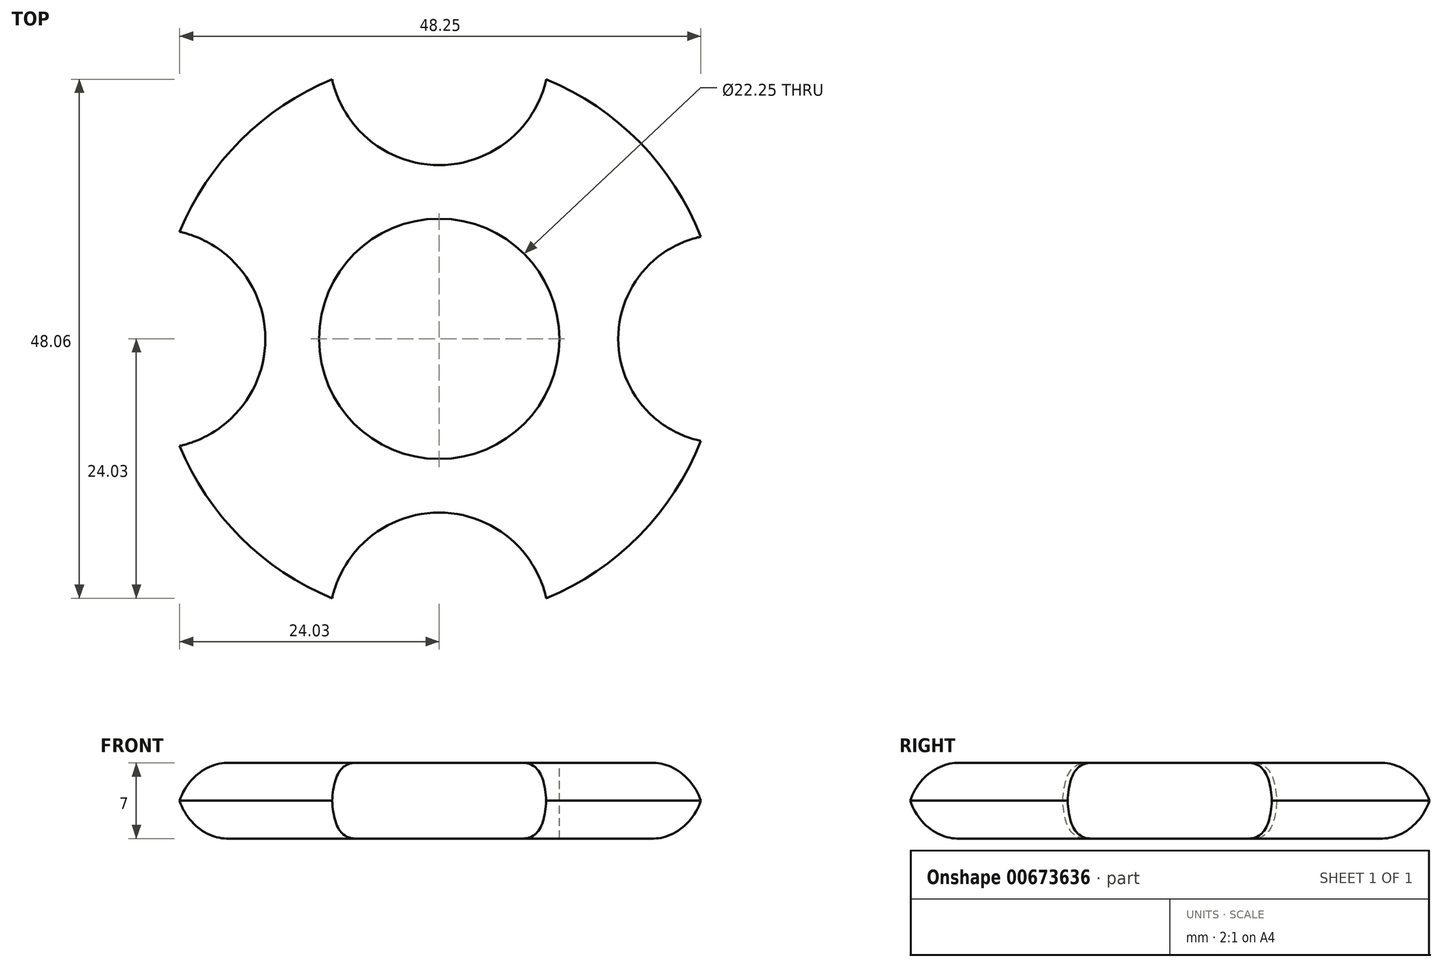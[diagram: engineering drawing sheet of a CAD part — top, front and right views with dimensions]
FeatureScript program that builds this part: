
annotation { "Feature Type Name" : "Feature", "Feature Type Description" : "" }
export const myFeature = defineFeature(function(context is Context, id is Id, definition is map)
    precondition{}
    {
        {
            var Q0;
            Q0=qCreatedBy(makeId("Top.planeOp"),FACE);
            var sketch = newSketch(context, id + "F0", { "sketchPlane" : qUnion([Q0])});
            skCircle(sketch, "E0", {"center": v(0, 0) * mm, "radius": 26.25 * mm});
            skSolve(sketch);
        }
        {
            var Q0;
            Q0 = qSketchRegion(id + "F0", true);
            extrude(context, id + "F1", {"entities" : qUnion([Q0]), "depth" : 7 * mm, "offsetDistance" : 25.4 * mm});
        }
        {
            var Q0;
            Q0=makeQuery(id+"F1.opExtrude","CAP_FACE",FACE,{"disambiguationData":[OSD([sQuery(id+"F0.wireOp",EDGE,"E0")])],"isStart":false});
            var sketch = newSketch(context, id + "F2", { "sketchPlane" : qUnion([Q0])});
            skCircle(sketch, "E1", {"center": v(0, 0) * mm, "radius": 11.13 * mm});
            skSolve(sketch);
        }
        {
            var Q0;
            Q0 = qSketchRegion(id + "F2", true);
            extrude(context, id + "F3", {"entities" : qUnion([Q0]), "operationType" : NewBodyOperationType.REMOVE, "oppositeDirection" : true, "depth" : 25.4 * mm, "offsetDistance" : 25.4 * mm});
        }
        {
            var Q0;
            Q0=makeQuery(id+"F1.opExtrude","CAP_FACE",FACE,{"disambiguationData":[OSD([sQuery(id+"F0.wireOp",EDGE,"E0")])],"isStart":false});
            var sketch = newSketch(context, id + "F4", { "sketchPlane" : qUnion([Q0])});
            skCircle(sketch, "E2", {"center": v(0, -26.25) * mm, "radius": 10.16 * mm});
            skCircle(sketch, "E3", {"center": v(-26.25, 0) * mm, "radius": 10.16 * mm});
            skCircle(sketch, "E4", {"center": v(0, 26.25) * mm, "radius": 10.16 * mm});
            skCircle(sketch, "E5", {"center": v(26.25, 0) * mm, "radius": 9.67 * mm});
            skSolve(sketch);
        }
        {
            var Q0;
            Q0 = qSketchRegion(id + "F4", true);
            extrude(context, id + "F5", {"entities" : qUnion([Q0]), "operationType" : NewBodyOperationType.REMOVE, "oppositeDirection" : true, "depth" : 25.4 * mm, "offsetDistance" : 25.4 * mm});
        }
        {
            var Q0;
            {var subQ0=sQuery(id+"F0.wireOp",EDGE,"E0");Q0=makeQuery(id+"F5.boolean.opBoolean","SPLIT",EDGE,{"disambiguationData":[TD([makeQuery(id+"F1.opExtrude","SWEPT_FACE",FACE,{"disambiguationData":[OSD([subQ0])]}),makeQuery(id+"F1.opExtrude","CAP_FACE",FACE,{"disambiguationData":[OSD([subQ0])],"isStart":true}),makeQuery(id+"F5.opExtrude","SWEPT_FACE",FACE,{"disambiguationData":[OSD([sQuery(id+"F4.wireOp",EDGE,"E2")])]}),makeQuery(id+"F5.opExtrude","SWEPT_FACE",FACE,{"disambiguationData":[OSD([sQuery(id+"F4.wireOp",EDGE,"E5")])]})])],"derivedFrom":makeQuery(id+"F1.opExtrude","CAP_EDGE",EDGE,{"disambiguationData":[OSD([subQ0])],"isStart":true})});}
            var Q1;
            {var subQ0=sQuery(id+"F0.wireOp",EDGE,"E0");Q1=makeQuery(id+"F5.boolean.opBoolean","SPLIT",EDGE,{"disambiguationData":[TD([makeQuery(id+"F1.opExtrude","SWEPT_FACE",FACE,{"disambiguationData":[OSD([subQ0])]}),makeQuery(id+"F1.opExtrude","CAP_FACE",FACE,{"disambiguationData":[OSD([subQ0])],"isStart":true}),makeQuery(id+"F5.opExtrude","SWEPT_FACE",FACE,{"disambiguationData":[OSD([sQuery(id+"F4.wireOp",EDGE,"E2")])]}),makeQuery(id+"F5.opExtrude","SWEPT_FACE",FACE,{"disambiguationData":[OSD([sQuery(id+"F4.wireOp",EDGE,"E3")])]})])],"derivedFrom":makeQuery(id+"F1.opExtrude","CAP_EDGE",EDGE,{"disambiguationData":[OSD([subQ0])],"isStart":true})});}
            var Q2;
            {var subQ0=sQuery(id+"F0.wireOp",EDGE,"E0");Q2=makeQuery(id+"F5.boolean.opBoolean","SPLIT",EDGE,{"disambiguationData":[TD([makeQuery(id+"F1.opExtrude","SWEPT_FACE",FACE,{"disambiguationData":[OSD([subQ0])]}),makeQuery(id+"F1.opExtrude","CAP_FACE",FACE,{"disambiguationData":[OSD([subQ0])],"isStart":true}),makeQuery(id+"F5.opExtrude","SWEPT_FACE",FACE,{"disambiguationData":[OSD([sQuery(id+"F4.wireOp",EDGE,"E3")])]}),makeQuery(id+"F5.opExtrude","SWEPT_FACE",FACE,{"disambiguationData":[OSD([sQuery(id+"F4.wireOp",EDGE,"E4")])]})])],"derivedFrom":makeQuery(id+"F1.opExtrude","CAP_EDGE",EDGE,{"disambiguationData":[OSD([subQ0])],"isStart":true})});}
            var Q3;
            {var subQ0=sQuery(id+"F0.wireOp",EDGE,"E0");Q3=makeQuery(id+"F5.boolean.opBoolean","SPLIT",EDGE,{"disambiguationData":[TD([makeQuery(id+"F1.opExtrude","SWEPT_FACE",FACE,{"disambiguationData":[OSD([subQ0])]}),makeQuery(id+"F1.opExtrude","CAP_FACE",FACE,{"disambiguationData":[OSD([subQ0])],"isStart":false}),makeQuery(id+"F5.opExtrude","SWEPT_FACE",FACE,{"disambiguationData":[OSD([sQuery(id+"F4.wireOp",EDGE,"E3")])]}),makeQuery(id+"F5.opExtrude","SWEPT_FACE",FACE,{"disambiguationData":[OSD([sQuery(id+"F4.wireOp",EDGE,"E4")])]})])],"derivedFrom":makeQuery(id+"F1.opExtrude","CAP_EDGE",EDGE,{"disambiguationData":[OSD([subQ0])],"isStart":false})});}
            var Q4;
            {var subQ0=sQuery(id+"F0.wireOp",EDGE,"E0");Q4=makeQuery(id+"F5.boolean.opBoolean","SPLIT",EDGE,{"disambiguationData":[TD([makeQuery(id+"F1.opExtrude","SWEPT_FACE",FACE,{"disambiguationData":[OSD([subQ0])]}),makeQuery(id+"F1.opExtrude","CAP_FACE",FACE,{"disambiguationData":[OSD([subQ0])],"isStart":false}),makeQuery(id+"F5.opExtrude","SWEPT_FACE",FACE,{"disambiguationData":[OSD([sQuery(id+"F4.wireOp",EDGE,"E2")])]}),makeQuery(id+"F5.opExtrude","SWEPT_FACE",FACE,{"disambiguationData":[OSD([sQuery(id+"F4.wireOp",EDGE,"E3")])]})])],"derivedFrom":makeQuery(id+"F1.opExtrude","CAP_EDGE",EDGE,{"disambiguationData":[OSD([subQ0])],"isStart":false})});}
            var Q5;
            {var subQ0=sQuery(id+"F0.wireOp",EDGE,"E0");Q5=makeQuery(id+"F5.boolean.opBoolean","SPLIT",EDGE,{"disambiguationData":[TD([makeQuery(id+"F1.opExtrude","SWEPT_FACE",FACE,{"disambiguationData":[OSD([subQ0])]}),makeQuery(id+"F1.opExtrude","CAP_FACE",FACE,{"disambiguationData":[OSD([subQ0])],"isStart":false}),makeQuery(id+"F5.opExtrude","SWEPT_FACE",FACE,{"disambiguationData":[OSD([sQuery(id+"F4.wireOp",EDGE,"E2")])]}),makeQuery(id+"F5.opExtrude","SWEPT_FACE",FACE,{"disambiguationData":[OSD([sQuery(id+"F4.wireOp",EDGE,"E5")])]})])],"derivedFrom":makeQuery(id+"F1.opExtrude","CAP_EDGE",EDGE,{"disambiguationData":[OSD([subQ0])],"isStart":false})});}
            var Q6;
            {var subQ0=sQuery(id+"F0.wireOp",EDGE,"E0");Q6=makeQuery(id+"F5.boolean.opBoolean","SPLIT",EDGE,{"disambiguationData":[TD([makeQuery(id+"F1.opExtrude","SWEPT_FACE",FACE,{"disambiguationData":[OSD([subQ0])]}),makeQuery(id+"F1.opExtrude","CAP_FACE",FACE,{"disambiguationData":[OSD([subQ0])],"isStart":false}),makeQuery(id+"F5.opExtrude","SWEPT_FACE",FACE,{"disambiguationData":[OSD([sQuery(id+"F4.wireOp",EDGE,"E4")])]}),makeQuery(id+"F5.opExtrude","SWEPT_FACE",FACE,{"disambiguationData":[OSD([sQuery(id+"F4.wireOp",EDGE,"E5")])]})])],"derivedFrom":makeQuery(id+"F1.opExtrude","CAP_EDGE",EDGE,{"disambiguationData":[OSD([subQ0])],"isStart":false})});}
            var Q7;
            {var subQ0=sQuery(id+"F0.wireOp",EDGE,"E0");Q7=makeQuery(id+"F5.boolean.opBoolean","SPLIT",EDGE,{"disambiguationData":[TD([makeQuery(id+"F1.opExtrude","SWEPT_FACE",FACE,{"disambiguationData":[OSD([subQ0])]}),makeQuery(id+"F1.opExtrude","CAP_FACE",FACE,{"disambiguationData":[OSD([subQ0])],"isStart":true}),makeQuery(id+"F5.opExtrude","SWEPT_FACE",FACE,{"disambiguationData":[OSD([sQuery(id+"F4.wireOp",EDGE,"E4")])]}),makeQuery(id+"F5.opExtrude","SWEPT_FACE",FACE,{"disambiguationData":[OSD([sQuery(id+"F4.wireOp",EDGE,"E5")])]})])],"derivedFrom":makeQuery(id+"F1.opExtrude","CAP_EDGE",EDGE,{"disambiguationData":[OSD([subQ0])],"isStart":true})});}
            fillet(context, id + "F6", {"entities" : qUnion([Q0, Q1, Q2, Q3, Q4, Q5, Q6, Q7]), "radius" : 5.08 * mm, "tangentPropagation" : true, "allowEdgeOverflow" : false});
        }
    });
